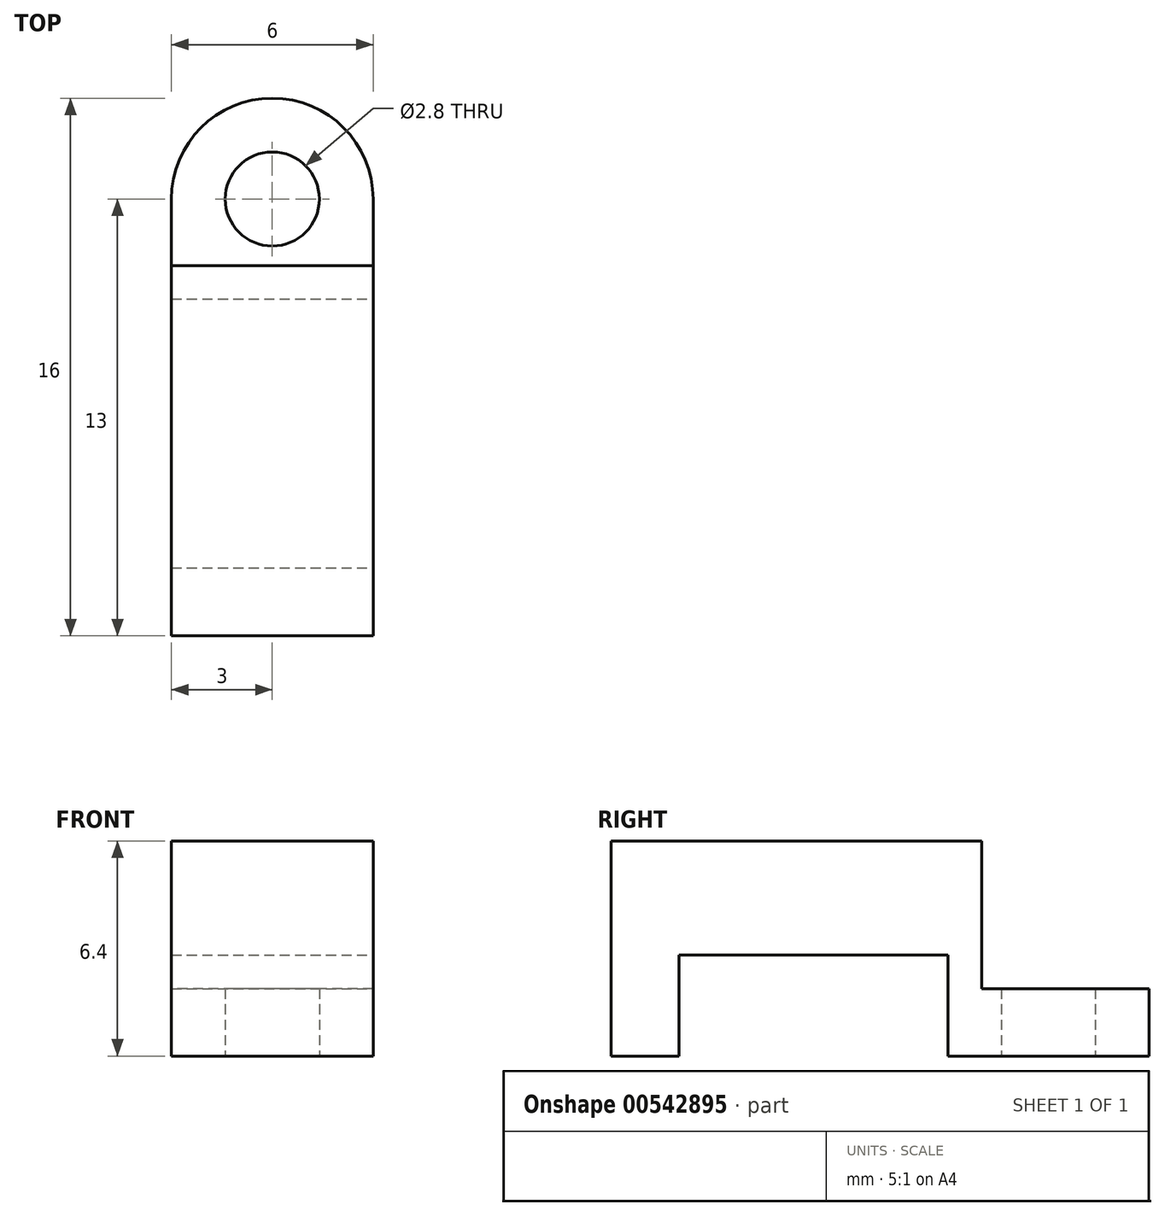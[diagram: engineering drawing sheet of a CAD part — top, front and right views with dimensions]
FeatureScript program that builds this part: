
annotation { "Feature Type Name" : "Feature", "Feature Type Description" : "" }
export const myFeature = defineFeature(function(context is Context, id is Id, definition is map)
    precondition{}
    {
        {
            var Q0;
            Q0=qCreatedBy(makeId("Top.planeOp"),FACE);
            var sketch = newSketch(context, id + "F0", { "sketchPlane" : qUnion([Q0])});
            skLineSegment(sketch, "E0.bottom", {"start": v(-3, 8) * mm, "end": v(3, 8) * mm});
            skLineSegment(sketch, "E0.top", {"start": v(-3, -8) * mm, "end": v(3, -8) * mm});
            skLineSegment(sketch, "E0.left", {"start": v(-3, 8) * mm, "end": v(-3, -8) * mm});
            skLineSegment(sketch, "E0.right", {"start": v(3, 8) * mm, "end": v(3, -8) * mm});
            skPoint(sketch, "E0.middle", {"position": v(0, 0) * mm});
            skCircle(sketch, "E1", {"center": v(0, 5) * mm, "radius": 1.4 * mm});
            skSolve(sketch);
        }
        {
            var Q0;
            Q0=makeQuery(id+"F0.imprint","IMPRINT",FACE,{"disambiguationData":[TD([[makeQuery(id+"F0.imprint","IMPRINT",EDGE,{"derivedFrom":sQuery(id+"F0.wireOp",EDGE,"E0.bottom")}),-1.0]])]});
            extrude(context, id + "F1", {"entities" : qUnion([Q0]), "depth" : 6.4 * mm, "offsetDistance" : 25 * mm});
        }
        {
            var Q0;
            Q0=makeQuery(id+"F1.opExtrude","SWEPT_EDGE",EDGE,{"disambiguationData":[OSD([sQuery(id+"F0.wireOp",EDGE,"E0.bottom"),sQuery(id+"F0.wireOp",EDGE,"E0.right")])]});
            var Q1;
            Q1=makeQuery(id+"F1.opExtrude","SWEPT_EDGE",EDGE,{"disambiguationData":[OSD([sQuery(id+"F0.wireOp",EDGE,"E0.bottom"),sQuery(id+"F0.wireOp",EDGE,"E0.left")])]});
            fillet(context, id + "F2", {"entities" : qUnion([Q0, Q1]), "tangentPropagation" : true, "radius" : 3 * mm, "defaultsChanged" : false, "vertexSettings" : [], "allowEdgeOverflow" : false});
        }
        {
            var Q0;
            Q0=makeQuery(id+"F1.opExtrude","SWEPT_FACE",FACE,{"disambiguationData":[OSD([sQuery(id+"F0.wireOp",EDGE,"E0.right")])]});
            var sketch = newSketch(context, id + "F3", { "sketchPlane" : qUnion([Q0])});
            skLineSegment(sketch, "E2.bottom", {"start": v(-5.98, 0) * mm, "end": v(2.02, 0) * mm});
            skLineSegment(sketch, "E2.top", {"start": v(-5.98, 3) * mm, "end": v(2.02, 3) * mm});
            skLineSegment(sketch, "E2.left", {"start": v(-5.98, 0) * mm, "end": v(-5.98, 3) * mm});
            skLineSegment(sketch, "E2.right", {"start": v(2.02, 0) * mm, "end": v(2.02, 3) * mm});
            skLineSegment(sketch, "E3", {"start": v(8.02, 0) * mm, "end": v(8.02, 2) * mm});
            skLineSegment(sketch, "E4.bottom", {"start": v(8.02, 7) * mm, "end": v(3.02, 7) * mm});
            skLineSegment(sketch, "E4.top", {"start": v(8.02, 2) * mm, "end": v(3.02, 2) * mm});
            skLineSegment(sketch, "E4.left", {"start": v(8.02, 7) * mm, "end": v(8.02, 2) * mm});
            skLineSegment(sketch, "E4.right", {"start": v(3.02, 7) * mm, "end": v(3.02, 2) * mm});
            skSolve(sketch);
        }
        {
            var Q0;
            {var subQ4=sQuery(id+"F3.wireOp",EDGE,"E4.right");Q0=makeQuery(id+"F3.imprint","IMPRINT",FACE,{"disambiguationData":[TD([[makeQuery(id+"F3.imprint","IMPRINT",EDGE,{"derivedFrom":subQ4}),1.0]])]});}
            var Q1;
            {var subQ4=sQuery(id+"F3.wireOp",EDGE,"E4.left");Q1=makeQuery(id+"F3.imprint","IMPRINT",FACE,{"disambiguationData":[TD([[makeQuery(id+"F3.imprint","IMPRINT",EDGE,{"derivedFrom":subQ4}),-1.0]])]});}
            var Q2;
            Q2=makeQuery(id+"F3.imprint","IMPRINT",FACE,{"disambiguationData":[TD([[makeQuery(id+"F3.imprint","IMPRINT",EDGE,{"derivedFrom":sQuery(id+"F3.wireOp",EDGE,"E2.bottom")}),-1.0]])]});
            extrude(context, id + "F4", {"entities" : qUnion([Q0, Q1, Q2]), "operationType" : NewBodyOperationType.REMOVE, "oppositeDirection" : true, "depth" : 8 * mm, "offsetDistance" : 25 * mm});
        }
    });
